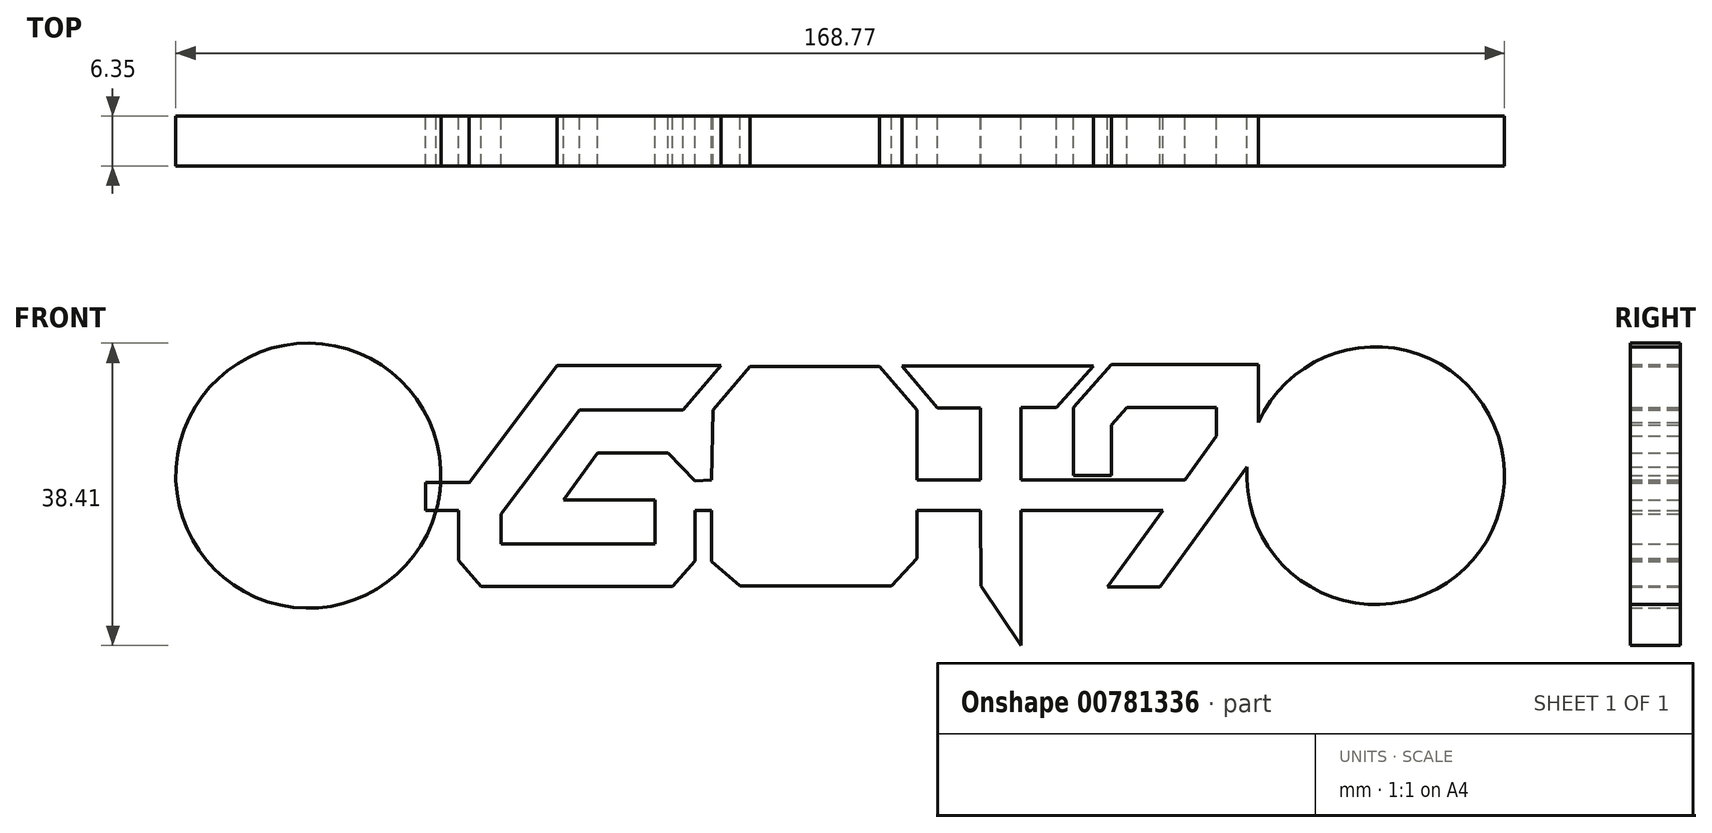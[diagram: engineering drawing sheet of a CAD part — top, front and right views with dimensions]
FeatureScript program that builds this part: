
annotation { "Feature Type Name" : "Feature", "Feature Type Description" : "" }
export const myFeature = defineFeature(function(context is Context, id is Id, definition is map)
    precondition{}
    {
        {
            var Q0;
            Q0=qCreatedBy(makeId("Front.planeOp"),FACE);
            var sketch = newSketch(context, id + "F0", { "sketchPlane" : qUnion([Q0])});
            skLineSegment(sketch, "E0", {"start": v(-12.49, 14) * mm, "end": v(-33.29, 14) * mm});
            skLineSegment(sketch, "E1", {"start": v(-33.29, 14) * mm, "end": v(-45.83, -2.75) * mm});
            skLineSegment(sketch, "E2", {"start": v(-45.83, -2.75) * mm, "end": v(-45.83, -10.75) * mm});
            skLineSegment(sketch, "E3", {"start": v(-12.49, 14) * mm, "end": v(-17.27, 8.37) * mm});
            skLineSegment(sketch, "E4", {"start": v(-17.27, 8.37) * mm, "end": v(-30.46, 8.37) * mm});
            skLineSegment(sketch, "E5", {"start": v(-30.46, 8.37) * mm, "end": v(-40.38, -4.9) * mm});
            skLineSegment(sketch, "E6", {"start": v(-40.38, -4.9) * mm, "end": v(-40.38, -8.69) * mm});
            skLineSegment(sketch, "E7", {"start": v(-40.38, -8.69) * mm, "end": v(-20.82, -8.69) * mm});
            skLineSegment(sketch, "E8", {"start": v(-20.82, -8.69) * mm, "end": v(-20.82, -3.08) * mm});
            skLineSegment(sketch, "E9", {"start": v(-20.82, -3.08) * mm, "end": v(-32.46, -3.08) * mm});
            skLineSegment(sketch, "E10", {"start": v(-32.46, -3.08) * mm, "end": v(-28.17, 2.86) * mm});
            skLineSegment(sketch, "E11", {"start": v(-28.17, 2.86) * mm, "end": v(-19.17, 2.86) * mm});
            skLineSegment(sketch, "E12", {"start": v(-19.17, 2.86) * mm, "end": v(-15.8, -0.68) * mm});
            skLineSegment(sketch, "E13", {"start": v(-15.8, -0.68) * mm, "end": v(-15.8, -10.84) * mm});
            skLineSegment(sketch, "E14", {"start": v(-45.83, -10.75) * mm, "end": v(-42.92, -14.1) * mm});
            skLineSegment(sketch, "E15", {"start": v(-42.92, -14.1) * mm, "end": v(-18.62, -14.1) * mm});
            skLineSegment(sketch, "E16", {"start": v(-18.62, -14.1) * mm, "end": v(-15.8, -10.84) * mm});
            skLineSegment(sketch, "E17", {"start": v(-13.48, 8.37) * mm, "end": v(-8.8, 13.87) * mm});
            skLineSegment(sketch, "E18", {"start": v(-8.8, 13.87) * mm, "end": v(7.69, 13.87) * mm});
            skLineSegment(sketch, "E19", {"start": v(7.69, 13.87) * mm, "end": v(12.46, 8.37) * mm});
            skLineSegment(sketch, "E20", {"start": v(12.46, 8.37) * mm, "end": v(12.46, -10.5) * mm});
            skLineSegment(sketch, "E21", {"start": v(12.46, -10.5) * mm, "end": v(9.16, -14.02) * mm});
            skLineSegment(sketch, "E22", {"start": v(9.16, -14.02) * mm, "end": v(-10.02, -14.02) * mm});
            skLineSegment(sketch, "E23", {"start": v(-10.02, -14.02) * mm, "end": v(-13.65, -10.88) * mm});
            skLineSegment(sketch, "E24", {"start": v(-13.65, -10.88) * mm, "end": v(-13.65, -0.52) * mm});
            skLineSegment(sketch, "E25", {"start": v(-13.65, -0.52) * mm, "end": v(-13.48, 8.37) * mm});
            skLineSegment(sketch, "E26", {"start": v(20.53, -14.02) * mm, "end": v(25.66, -21.58) * mm});
            skLineSegment(sketch, "E27", {"start": v(25.66, -21.58) * mm, "end": v(25.66, 8.64) * mm});
            skLineSegment(sketch, "E28", {"start": v(25.66, 8.64) * mm, "end": v(30.16, 8.64) * mm});
            skLineSegment(sketch, "E29", {"start": v(30.16, 8.64) * mm, "end": v(34.82, 13.95) * mm});
            skLineSegment(sketch, "E30", {"start": v(34.82, 13.95) * mm, "end": v(10.55, 13.95) * mm});
            skLineSegment(sketch, "E31", {"start": v(10.55, 13.95) * mm, "end": v(15.04, 8.58) * mm});
            skLineSegment(sketch, "E32", {"start": v(15.04, 8.58) * mm, "end": v(20.47, 8.58) * mm});
            skLineSegment(sketch, "E33", {"start": v(20.53, -14.02) * mm, "end": v(20.47, 8.58) * mm});
            skLineSegment(sketch, "E34", {"start": v(36.63, -14.13) * mm, "end": v(43.3, -14.13) * mm});
            skLineSegment(sketch, "E35", {"start": v(43.3, -14.13) * mm, "end": v(55.77, 3.04) * mm});
            skLineSegment(sketch, "E36", {"start": v(55.77, 3.04) * mm, "end": v(55.77, 14.13) * mm});
            skLineSegment(sketch, "E37", {"start": v(55.77, 14.13) * mm, "end": v(37.12, 14.13) * mm});
            skLineSegment(sketch, "E38", {"start": v(37.12, 14.13) * mm, "end": v(32.3, 8.64) * mm});
            skLineSegment(sketch, "E39", {"start": v(32.3, 8.64) * mm, "end": v(32.3, 0) * mm});
            skLineSegment(sketch, "E40", {"start": v(32.3, 0) * mm, "end": v(37.12, 0) * mm});
            skLineSegment(sketch, "E41", {"start": v(37.12, 0) * mm, "end": v(37.12, 6.4) * mm});
            skLineSegment(sketch, "E42", {"start": v(37.12, 6.4) * mm, "end": v(39.08, 8.64) * mm});
            skLineSegment(sketch, "E43", {"start": v(39.08, 8.64) * mm, "end": v(50.47, 8.64) * mm});
            skLineSegment(sketch, "E44", {"start": v(50.47, 8.64) * mm, "end": v(50.47, 5) * mm});
            skLineSegment(sketch, "E45", {"start": v(50.47, 5) * mm, "end": v(36.63, -14.13) * mm});
            skLineSegment(sketch, "E46", {"start": v(-15.8, -0.68) * mm, "end": v(-13.65, -0.52) * mm});
            skLineSegment(sketch, "E47", {"start": v(-13.65, -0.52) * mm, "end": v(46.47, -0.52) * mm});
            skLineSegment(sketch, "E48", {"start": v(-15.8, -4.43) * mm, "end": v(43.65, -4.43) * mm});
            skLineSegment(sketch, "E49", {"start": v(-45.83, -2.75) * mm, "end": v(-45.83, 14) * mm, "construction": true});
            skSolve(sketch);
        }
        {
            var Q0;
            Q0=makeQuery(id+"F0.imprint","IMPRINT",FACE,{"disambiguationData":[TD([[makeQuery(id+"F0.imprint","IMPRINT",EDGE,{"derivedFrom":sQuery(id+"F0.wireOp",EDGE,"E0")}),1.0]])]});
            var Q1;
            {var subQ0=sQuery(id+"F0.wireOp",EDGE,"E46");Q1=makeQuery(id+"F0.imprint","IMPRINT",FACE,{"disambiguationData":[TD([[makeQuery(id+"F0.imprint","IMPRINT",EDGE,{"derivedFrom":subQ0}),-1.0]])]});}
            var Q2;
            Q2=makeQuery(id+"F0.imprint","IMPRINT",FACE,{"disambiguationData":[TD([[makeQuery(id+"F0.imprint","IMPRINT",EDGE,{"derivedFrom":sQuery(id+"F0.wireOp",EDGE,"E17")}),-1.0]])]});
            var Q3;
            {var subQ1=sQuery(id+"F0.wireOp",EDGE,"E21");Q3=makeQuery(id+"F0.imprint","IMPRINT",FACE,{"disambiguationData":[TD([[makeQuery(id+"F0.imprint","IMPRINT",EDGE,{"derivedFrom":subQ1}),-1.0]])]});}
            var Q4;
            {var subQ0=sQuery(id+"F0.wireOp",EDGE,"E47");var subQ1=sQuery(id+"F0.wireOp",EDGE,"E20");var subQ2=makeQuery(id+"F0.imprint","INTERSECT",VERTEX,{"derivedFrom":[subQ1,subQ0]});Q4=makeQuery(id+"F0.imprint","IMPRINT",FACE,{"disambiguationData":[TD([[makeQuery(id+"F0.imprint","IMPRINT",EDGE,{"disambiguationData":[TD([[subQ2,-1.0]])],"derivedFrom":subQ1}),-1.0]])]});}
            var Q5;
            {var subQ0=sQuery(id+"F0.wireOp",EDGE,"E47");var subQ1=sQuery(id+"F0.wireOp",EDGE,"E20");var subQ2=makeQuery(id+"F0.imprint","INTERSECT",VERTEX,{"derivedFrom":[subQ1,subQ0]});Q5=makeQuery(id+"F0.imprint","IMPRINT",FACE,{"disambiguationData":[TD([[makeQuery(id+"F0.imprint","IMPRINT",EDGE,{"disambiguationData":[TD([[subQ2,-1.0]])],"derivedFrom":subQ1}),1.0]])]});}
            var Q6;
            {var subQ0=sQuery(id+"F0.wireOp",EDGE,"E48");var subQ1=sQuery(id+"F0.wireOp",EDGE,"E27");var subQ2=makeQuery(id+"F0.imprint","INTERSECT",VERTEX,{"derivedFrom":[subQ1,subQ0]});Q6=makeQuery(id+"F0.imprint","IMPRINT",FACE,{"disambiguationData":[TD([[makeQuery(id+"F0.imprint","IMPRINT",EDGE,{"disambiguationData":[TD([[subQ2,-1.0]])],"derivedFrom":subQ1}),1.0]])]});}
            var Q7;
            {var subQ0=sQuery(id+"F0.wireOp",EDGE,"E26");Q7=makeQuery(id+"F0.imprint","IMPRINT",FACE,{"disambiguationData":[TD([[makeQuery(id+"F0.imprint","IMPRINT",EDGE,{"derivedFrom":subQ0}),1.0]])]});}
            var Q8;
            {var subQ0=sQuery(id+"F0.wireOp",EDGE,"E28");Q8=makeQuery(id+"F0.imprint","IMPRINT",FACE,{"disambiguationData":[TD([[makeQuery(id+"F0.imprint","IMPRINT",EDGE,{"derivedFrom":subQ0}),1.0]])]});}
            var Q9;
            {var subQ0=sQuery(id+"F0.wireOp",EDGE,"E48");var subQ1=sQuery(id+"F0.wireOp",EDGE,"E27");var subQ2=makeQuery(id+"F0.imprint","INTERSECT",VERTEX,{"derivedFrom":[subQ1,subQ0]});Q9=makeQuery(id+"F0.imprint","IMPRINT",FACE,{"disambiguationData":[TD([[makeQuery(id+"F0.imprint","IMPRINT",EDGE,{"disambiguationData":[TD([[subQ2,-1.0]])],"derivedFrom":subQ1}),-1.0]])]});}
            var Q10;
            {var subQ0=sQuery(id+"F0.wireOp",EDGE,"E34");Q10=makeQuery(id+"F0.imprint","IMPRINT",FACE,{"disambiguationData":[TD([[makeQuery(id+"F0.imprint","IMPRINT",EDGE,{"derivedFrom":subQ0}),1.0]])]});}
            extrude(context, id + "F1", {"entities" : qUnion([Q0, Q1, Q2, Q3, Q4, Q5, Q6, Q7, Q8, Q9, Q10]), "depth" : 6.35 * mm, "offsetDistance" : 25.4 * mm});
        }
        {
            var Q0;
            Q0=qCreatedBy(makeId("Front.planeOp"),FACE);
            var sketch = newSketch(context, id + "F2", { "sketchPlane" : qUnion([Q0])});
            skCircle(sketch, "E50", {"center": v(-64.88, 0) * mm, "radius": 16.83 * mm});
            skCircle(sketch, "E51", {"center": v(70.68, 0) * mm, "radius": 16.37 * mm});
            skLineSegment(sketch, "E52", {"start": v(-15.74, -4.45) * mm, "end": v(-17.33, -4.45) * mm});
            skLineSegment(sketch, "E53", {"start": v(-17.33, -4.45) * mm, "end": v(-49.98, -4.45) * mm});
            skLineSegment(sketch, "E54", {"start": v(-49.98, -4.45) * mm, "end": v(-49.98, -0.86) * mm});
            skLineSegment(sketch, "E55", {"start": v(-49.98, -0.86) * mm, "end": v(-14.28, -0.86) * mm});
            skLineSegment(sketch, "E56", {"start": v(-15.74, -4.45) * mm, "end": v(-14.28, -0.86) * mm});
            skLineSegment(sketch, "E57", {"start": v(-44.47, -4.45) * mm, "end": v(-44.47, -0.86) * mm});
            skLineSegment(sketch, "E58", {"start": v(-48.65, -4.45) * mm, "end": v(-48.65, -0.86) * mm});
            skSolve(sketch);
        }
        {
            var Q0;
            {var subQ5=sQuery(id+"F2.wireOp",EDGE,"E57");Q0=makeQuery(id+"F2.imprint","IMPRINT",FACE,{"disambiguationData":[TD([[makeQuery(id+"F2.imprint","IMPRINT",EDGE,{"derivedFrom":subQ5}),1.0]])]});}
            var Q1;
            {var subQ5=sQuery(id+"F2.wireOp",EDGE,"E54");Q1=makeQuery(id+"F2.imprint","IMPRINT",FACE,{"disambiguationData":[TD([[makeQuery(id+"F2.imprint","IMPRINT",EDGE,{"derivedFrom":subQ5}),1.0]])]});}
            var Q2;
            Q2=makeQuery(id+"F2.imprint","IMPRINT",FACE,{"disambiguationData":[TD([[makeQuery(id+"F2.imprint","IMPRINT",EDGE,{"derivedFrom":sQuery(id+"F2.wireOp",EDGE,"E51")}),1.0]])]});
            extrude(context, id + "F3", {"entities" : qUnion([Q0, Q1, Q2]), "operationType" : NewBodyOperationType.ADD, "depth" : 6.35 * mm, "offsetDistance" : 25.4 * mm});
        }
        {
            var Q0;
            {var subQ0=sQuery(id+"F2.wireOp",EDGE,"E54");Q0=makeQuery(id+"F2.imprint","IMPRINT",FACE,{"disambiguationData":[TD([[makeQuery(id+"F2.imprint","IMPRINT",EDGE,{"derivedFrom":subQ0}),-1.0]])]});}
            var Q1;
            {var subQ0=sQuery(id+"F2.wireOp",EDGE,"E58");Q1=makeQuery(id+"F2.imprint","IMPRINT",FACE,{"disambiguationData":[TD([[makeQuery(id+"F2.imprint","IMPRINT",EDGE,{"derivedFrom":subQ0}),-1.0]])]});}
            extrude(context, id + "F4", {"entities" : qUnion([Q0, Q1]), "depth" : 6.35 * mm, "offsetDistance" : 25.4 * mm});
        }
    });
